# Revit family: QF_TRUE_TS-49F-HC_cat
name_source: partatom
category: Specialty Equipment
revit_build: Autodesk Revit 2014 (Build: 20130308_1515(x64)
units: mm (PartAtom-declared; Revit-internal decimal feet)

## types (1)
- QF_TRUE_TS-49F-HC_cat
    Apparent Power = 1104 VA
    Body Finish = QF_Finishes_Stainless Steel
    Conn Conduit = Yes
    Conn Plug = NEMA-5-15P
    Cycle = 60 Hz
    Depth = 29 1/2"
    Description = REACH-IN SOLID SWING DOOR STAINLESS STEEL FREEZER WITH HYDROCARBON REFRIGERANT
    FL Amps = 10 A
    HP = 1/2
    Height = 83 5/16"
    Manufacturer = TRUE FOOD SERVICE EQUIPMENT, INC.
    Max Overcurrent Protection = 0 A
    Min Ckt Ampacity = 0 A
    Model = TS-49F-HC
    Phase = 1
    Type Comments = www.truemfg.com
    URL = www.truemfg.com
    URL Cutsheet = www.truemfg.com
    URL Manufacturer = www.truemfg.com
    Volts = 115 V
    Watts = 1104 W
    Weight = 440
    Width = 54 1/8"

## geometry (parser evidence)
native form markers: Blend x37, Sweep x4
no freeform markers — native parametric forms only
